# Revit family: Haworth_Veda_Chair_Task_MidBack_PRELIMINARY
name_source: partatom
category: Furniture
revit_build: Autodesk Revit 2018 (Build: 20170223_1515(x64)
units: mm (PartAtom-declared; Revit-internal decimal feet)

## family parameters
Always vertical = Yes
Cut with Voids When Loaded = No
OmniClass Number = 23.40.70.14.64.11
OmniClass Title = Office Furniture
Room Calculation Point = No
Shared = No
Work Plane-Based = No

## types (2) — shared parameters
Actual Depth = 28 "
Actual Height = 40 "
Actual Width = 28 "
Assembly Code = E2020200
Description = Task Chair - Mid Back
Manufacturer = Haworth
Model = Haworth - Chair - Veda
Revision Number = 1
Size = Verify Final Dim. w/ Haworth
Sustainability Info = https://www.haworth.com
URL = https://www.haworth.com
URL - Product = https://www.haworth.com
Warranty = http://www.haworth.com

## per-type parameters (varying)
| type | Standard Tilt | Synchronized Tilt |
| Mid - Back Chair - Synchronized Tilt | No | Yes |
| Mid - Back Chair - Standard Tilt | Yes | No |

## geometry (parser evidence)
native form markers: Sweep x12
no freeform markers — native parametric forms only
